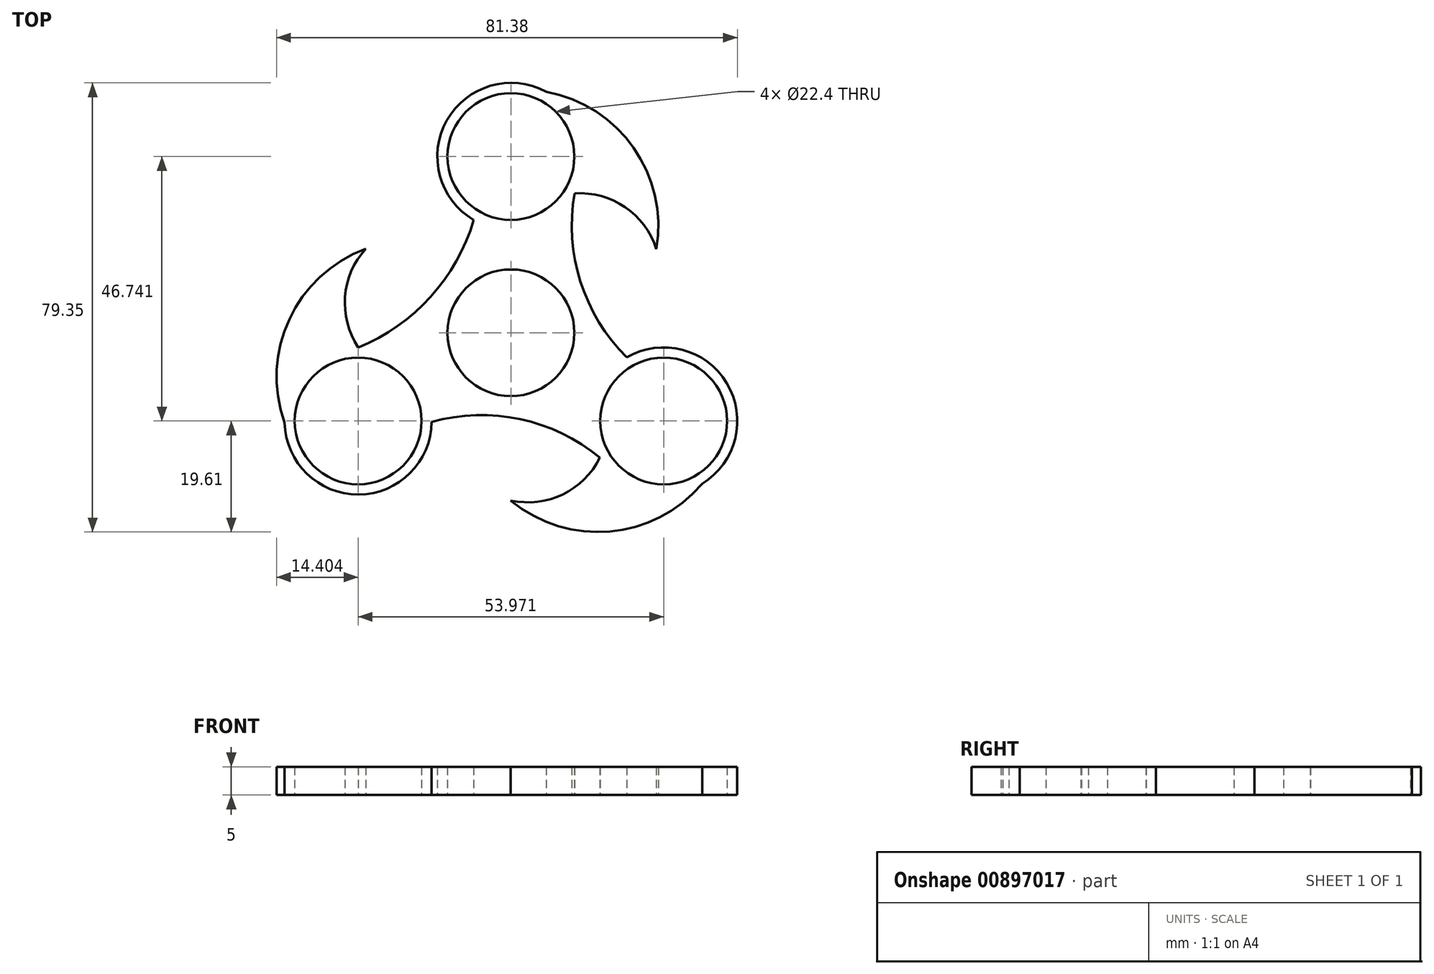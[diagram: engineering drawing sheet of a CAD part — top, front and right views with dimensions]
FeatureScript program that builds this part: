
annotation { "Feature Type Name" : "Feature", "Feature Type Description" : "" }
export const myFeature = defineFeature(function(context is Context, id is Id, definition is map)
    precondition{}
    {
        {
            var Q0;
            Q0=qCreatedBy(makeId("Top.planeOp"),FACE);
            var sketch = newSketch(context, id + "F0", { "sketchPlane" : qUnion([Q0])});
            skCircle(sketch, "E0", {"center": v(0, 0) * mm, "radius": 11.2 * mm});
            skCircle(sketch, "E1", {"center": v(0, 31.16) * mm, "radius": 11.2 * mm});
            skCircle(sketch, "E2", {"center": v(0, 31.16) * mm, "radius": 13 * mm});
            skCircle(sketch, "E3.1.0", {"center": v(-26.99, -15.58) * mm, "radius": 13 * mm});
            skCircle(sketch, "E4.1.0", {"center": v(-26.99, -15.58) * mm, "radius": 11.2 * mm});
            skCircle(sketch, "E4.2.0", {"center": v(26.99, -15.58) * mm, "radius": 11.2 * mm});
            skCircle(sketch, "E4.2.1", {"center": v(26.99, -15.58) * mm, "radius": 13 * mm});
            skArc(sketch, "E5", {"start": v(25.69, 14.79) * mm, "mid": v(21.66, 32.7) * mm, "end": v(6.2, 42.58) * mm});
            skArc(sketch, "E6", {"start": v(25.69, 14.79) * mm, "mid": v(20.16, 22.2) * mm, "end": v(11.24, 24.63) * mm});
            skArc(sketch, "E7.1.0", {"start": v(-25.64, 14.85) * mm, "mid": v(-29.3, 6.36) * mm, "end": v(-26.94, -2.58) * mm});
            skArc(sketch, "E7.1.1", {"start": v(-25.64, 14.85) * mm, "mid": v(-39.13, 2.41) * mm, "end": v(-39.97, -15.92) * mm});
            skArc(sketch, "E7.2.0", {"start": v(-0.03, -29.63) * mm, "mid": v(9.15, -28.56) * mm, "end": v(15.72, -22.04) * mm});
            skArc(sketch, "E7.2.1", {"start": v(-0.03, -29.63) * mm, "mid": v(17.49, -35.1) * mm, "end": v(33.78, -26.66) * mm});
            skArc(sketch, "E8", {"start": v(-26.94, -2.58) * mm, "mid": v(-14.2, 6.36) * mm, "end": v(-6.57, 19.94) * mm});
            skArc(sketch, "E9.1.0", {"start": v(15.72, -22.04) * mm, "mid": v(1.64, -15.26) * mm, "end": v(-13.99, -15.73) * mm});
            skArc(sketch, "E9.2.0", {"start": v(11.24, 24.63) * mm, "mid": v(12.38, 8.77) * mm, "end": v(20.8, -4.72) * mm});
            skSolve(sketch);
        }
        {
            var Q0;
            Q0 = qSketchRegion(id + "F0", true);
            extrude(context, id + "F1", {"entities" : qUnion([Q0]), "depth" : 5 * mm, "offsetDistance" : 25 * mm});
        }
    });
